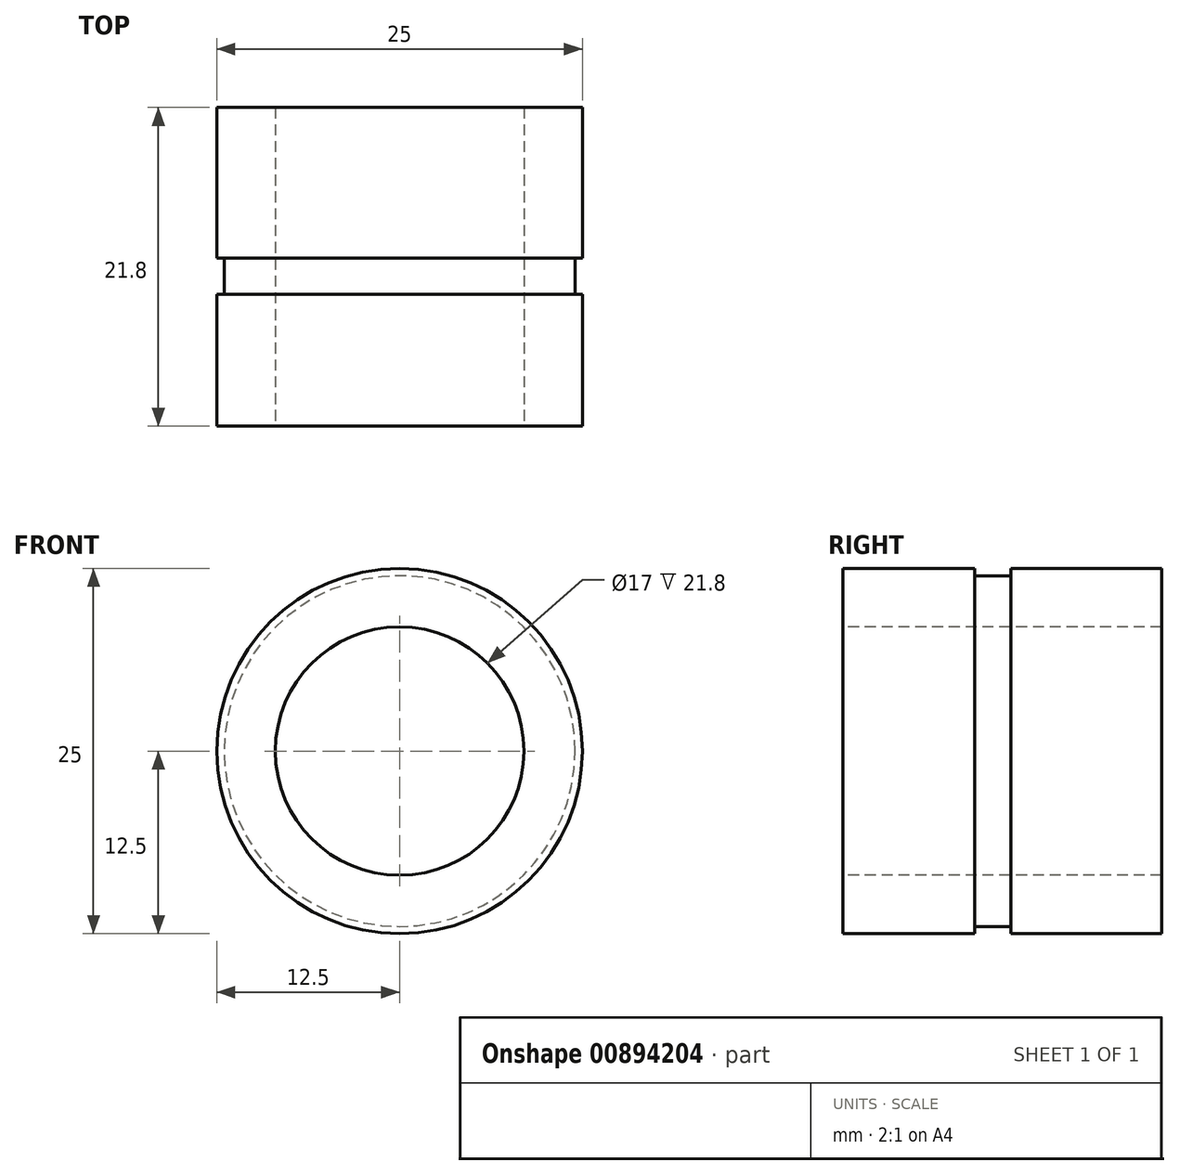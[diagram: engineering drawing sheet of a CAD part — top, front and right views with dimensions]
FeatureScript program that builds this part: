
annotation { "Feature Type Name" : "Feature", "Feature Type Description" : "" }
export const myFeature = defineFeature(function(context is Context, id is Id, definition is map)
    precondition{}
    {
        {
            var Q0;
            Q0=qCreatedBy(makeId("Right.planeOp"),FACE);
            var sketch = newSketch(context, id + "F0", { "sketchPlane" : qUnion([Q0])});
            skLineSegment(sketch, "E0", {"start": v(0, 0) * mm, "end": v(0, 8.5) * mm, "construction": true});
            skLineSegment(sketch, "E1", {"start": v(0, 8.5) * mm, "end": v(21.8, 8.5) * mm});
            skLineSegment(sketch, "E2", {"start": v(21.8, 8.5) * mm, "end": v(21.8, 12.5) * mm});
            skLineSegment(sketch, "E3", {"start": v(0, 12.5) * mm, "end": v(0, 8.5) * mm});
            skLineSegment(sketch, "E4", {"start": v(0, 12.5) * mm, "end": v(9, 12.5) * mm});
            skLineSegment(sketch, "E5", {"start": v(9, 12.5) * mm, "end": v(9, 12) * mm});
            skLineSegment(sketch, "E6", {"start": v(9, 12) * mm, "end": v(11.5, 12) * mm});
            skLineSegment(sketch, "E7", {"start": v(11.5, 12) * mm, "end": v(11.5, 12.5) * mm});
            skLineSegment(sketch, "E8", {"start": v(11.5, 12.5) * mm, "end": v(21.8, 12.5) * mm});
            skLineSegment(sketch, "E9", {"start": v(0, 0) * mm, "end": v(21.8, 0) * mm});
            skSolve(sketch);
        }
        {
            var Q0;
            Q0 = qSketchRegion(id + "F0", true);
            var Q1;
            Q1=sQuery(id+"F0.wireOp",EDGE,"E9");
            revolve(context, id + "F1", {"surfaceOperationType" : NewSurfaceOperationType.NEW, "entities" : qUnion([Q0]), "axis" : qUnion([Q1]), "revolveType" : RevolveType.FULL});
        }
    });
